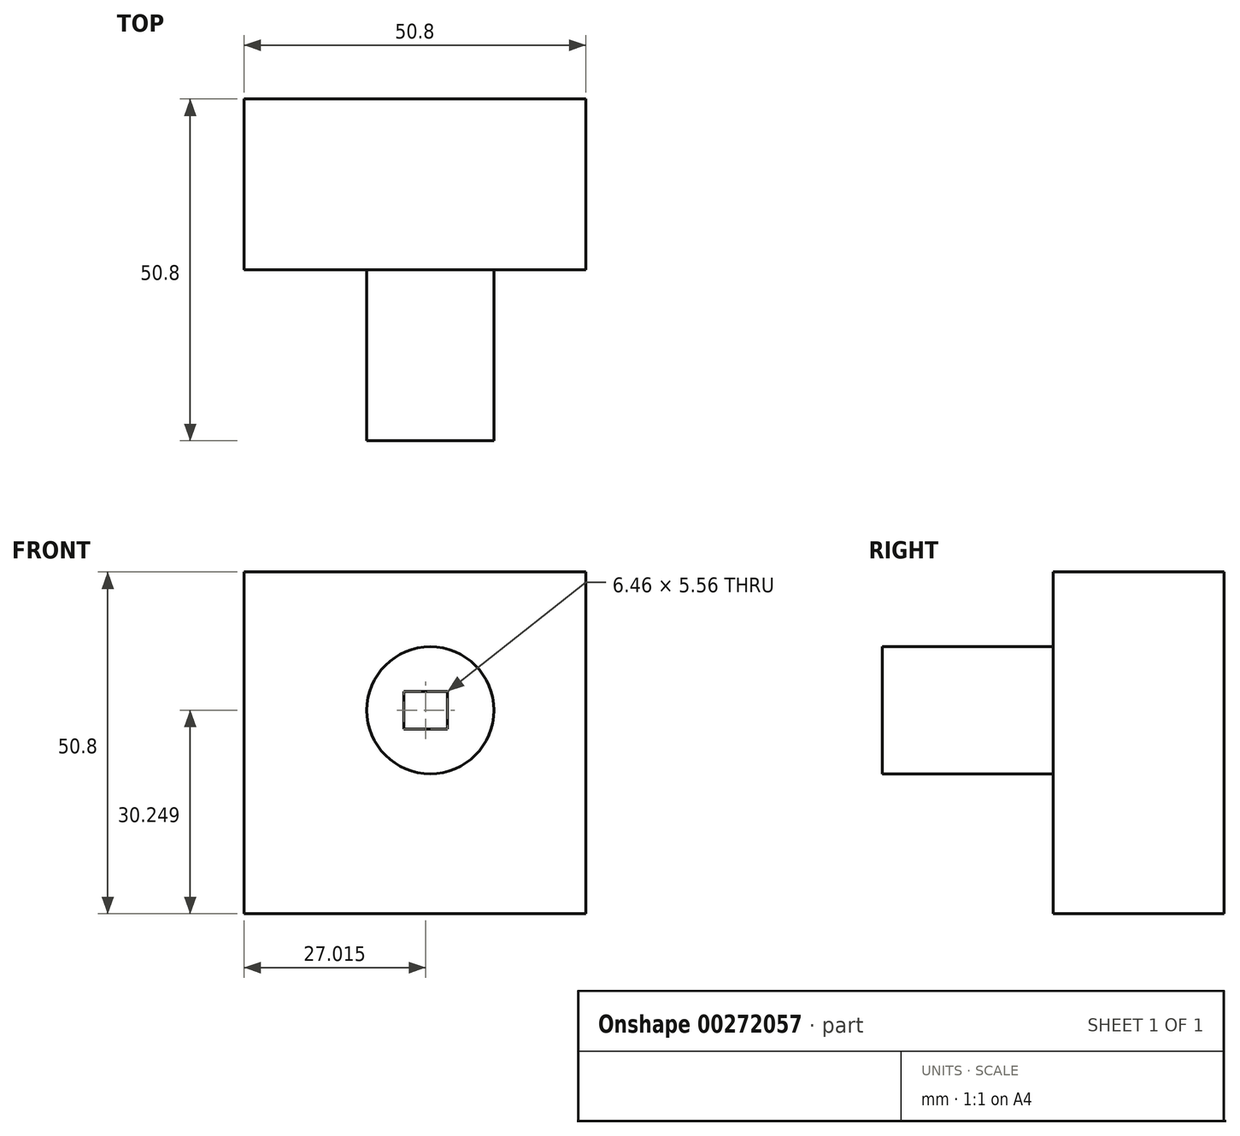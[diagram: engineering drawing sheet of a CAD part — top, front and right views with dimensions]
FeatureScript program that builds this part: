
annotation { "Feature Type Name" : "Feature", "Feature Type Description" : "" }
export const myFeature = defineFeature(function(context is Context, id is Id, definition is map)
    precondition{}
    {
        {
            var Q0;
            Q0=qCreatedBy(makeId("Front.planeOp"),FACE);
            var sketch = newSketch(context, id + "F0", { "sketchPlane" : qUnion([Q0])});
            skLineSegment(sketch, "E0", {"start": v(-45.24, 23.33) * mm, "end": v(-45.24, -27.47) * mm});
            skLineSegment(sketch, "E1", {"start": v(-45.24, 23.33) * mm, "end": v(5.56, 23.33) * mm});
            skLineSegment(sketch, "E2", {"start": v(5.56, 23.33) * mm, "end": v(5.56, -27.47) * mm});
            skLineSegment(sketch, "E3", {"start": v(-45.24, -27.47) * mm, "end": v(5.56, -27.47) * mm});
            skLineSegment(sketch, "E4.bottom", {"start": v(-21.46, 0) * mm, "end": v(-15, 0) * mm});
            skLineSegment(sketch, "E4.top", {"start": v(-21.46, 5.56) * mm, "end": v(-15, 5.56) * mm});
            skLineSegment(sketch, "E4.left", {"start": v(-21.46, 0) * mm, "end": v(-21.46, 5.56) * mm});
            skLineSegment(sketch, "E4.right", {"start": v(-15, 0) * mm, "end": v(-15, 5.56) * mm});
            skSolve(sketch);
        }
        {
            var Q0;
            Q0=makeQuery(id+"F0.imprint","IMPRINT",FACE,{"disambiguationData":[TD([[makeQuery(id+"F0.imprint","IMPRINT",EDGE,{"derivedFrom":sQuery(id+"F0.wireOp",EDGE,"E0")}),1.0]])]});
            extrude(context, id + "F1", {"entities" : qUnion([Q0]), "depth" : 25.4 * mm});
        }
        {
            var Q0;
            Q0=makeQuery(id+"F1.opExtrude","CAP_FACE",FACE,{"disambiguationData":[OSD([sQuery(id+"F0.wireOp",EDGE,"E0"),sQuery(id+"F0.wireOp",EDGE,"E1"),sQuery(id+"F0.wireOp",EDGE,"E2"),sQuery(id+"F0.wireOp",EDGE,"E3"),sQuery(id+"F0.wireOp",EDGE,"E4.bottom"),sQuery(id+"F0.wireOp",EDGE,"E4.top"),sQuery(id+"F0.wireOp",EDGE,"E4.left"),sQuery(id+"F0.wireOp",EDGE,"E4.right")])],"isStart":false});
            var sketch = newSketch(context, id + "F2", { "sketchPlane" : qUnion([Q0])});
            skCircle(sketch, "E5", {"center": v(-17.54, 2.78) * mm, "radius": 9.44 * mm});
            skPoint(sketch, "E5.centerSnap0", {"position": v(-15, 2.78) * mm});
            skSolve(sketch);
        }
        {
            var Q0;
            Q0 = qSketchRegion(id + "F2", true);
            extrude(context, id + "F3", {"entities" : qUnion([Q0]), "operationType" : NewBodyOperationType.ADD, "depth" : 25.4 * mm});
        }
        {
            var Q0;
            Q0=makeQuery(id+"F0.imprint","IMPRINT",FACE,{"disambiguationData":[TD([[makeQuery(id+"F0.imprint","IMPRINT",EDGE,{"derivedFrom":sQuery(id+"F0.wireOp",EDGE,"E4.bottom")}),1.0]])]});
            extrude(context, id + "F4", {"entities" : qUnion([Q0]), "operationType" : NewBodyOperationType.REMOVE, "endBound" : BoundingType.THROUGH_ALL, "depth" : 25.4 * mm});
        }
    });
